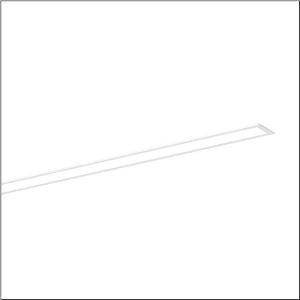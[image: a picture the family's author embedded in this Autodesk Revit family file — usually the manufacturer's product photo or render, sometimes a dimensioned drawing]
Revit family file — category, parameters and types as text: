
# Revit family: silica_r__21_51mx10dc45wb_eef5
name_source: partatom
category: Lighting Fixtures
units: mm (PartAtom-declared; Revit-internal decimal feet)

## family parameters
Cut with Voids When Loaded = No
Host = Face
Light Source = No
Part Type = Normal
Room Calculation Point = No
Round Connector Dimension = Use Diameter
Shared = No

## types (1)
- --- (1 x LED, 6000 lm, 40.1 W, 4000K)
    Apparent Load = 40 VA
    CIE Flux Codes = 48 79 96 100 100
    Color Rendering = 80
    Color Temperature = 4000K
    Default Elevation = 1800 mm
    Description = Silica® 21, office luminaire, primary optical cover: cover, of PMMA, opal, light emission: direct distribution, primary light characteristic: symmetric, installation type: recessed, LED, rated luminous flux: 6.000lm, luminous efficacy: 150lm/W, light colour: 840, colour temperature: 4000K, with terminal, 3+2-pole, max. 2.5mm², mains connection: 220..240V, AC, 50/60Hz, rated input power: 40.1W, luminaire housing, of aluminium, traffic white (RAL 9016), length: 3.028mm, width: 79mm, height: 53mm, protection rating (complete): IP20, insulation class (complete): insulation class I (protective earthing), certification: CE, permissible operating ambient temperature: 0..+35°C, standard: EN 50419, packaging unit: 1 piece
    Height = 0 mm  [stored 0 ft]
    Lamp = 1 x LED
    Lamp Light Flux = 6000 lm
    Lamp Power = 40.1 W
    Lamp count = 1
    Length = 3027 mm
    Luminous efficacy = 150 lm/W
    Manufacturer = Siteco
    ModVariant = No
    Model = 51MX10DC45WB
    Mounting Place = Ceiling
    Mounting Type = Recessed
    Number of Poles = 1
    OnlyDefault = Yes
    Power Factor = 1
    Product Name = Silica® 21
    Product group = office luminaire | ceiling recessed
    ProductGroupID = 400
    Protection Class = Protection class I
    Protection Degree = IP 20
    RLX_Detail_Level = 1
    RLX_Emergency_Light_Flux = 0 lm
    RLX_Emergency_Type = 0
    RLX_Emergency_Type_DB = No
    RlxData = <blob elided: 21213 chars, md5=c228e6e2>
    Socket = socket
    Standby Power = 0 W
    System Light Flux = 6000 lm
    System Power = 40 W
    Type Comments = factory setting: luminous flux: 100 % | dim-lin: 254 | 218 mA
    Type Image = l_1335891.jpg
    URL = http://relux.com
    VarID = @adj_086401
    Voltage = 0 V
    Weight = 0.00 kg
    Width = 79 mm

note: [stored X ft] marks values corroborated as IEEE doubles in the binary element streams (Revit-internal decimal feet)

## geometry (parser evidence)
native form markers: Blend x4, Sweep x12
no freeform markers — native parametric forms only
